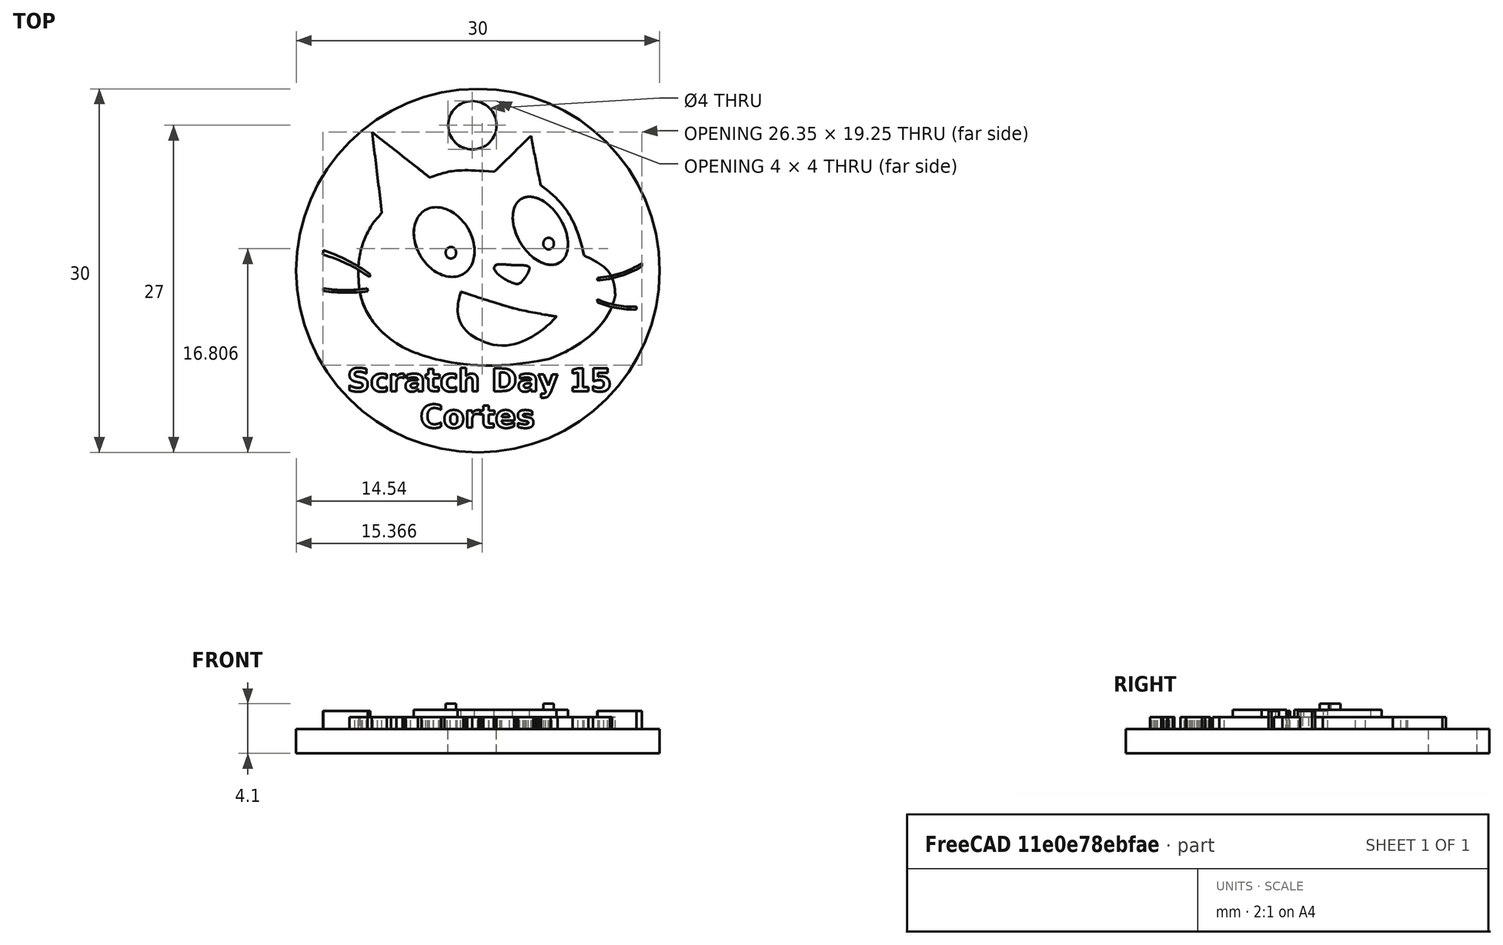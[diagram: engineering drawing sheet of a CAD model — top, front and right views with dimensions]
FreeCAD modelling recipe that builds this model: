
FCSTD DOCUMENT  (FreeCAD 0.14R3702 (Git))
Label: miscratch
License: CC-BY 3.0
LicenseURL: http://creativecommons.org/licenses/by/3.0/
objects: Part::Extrusion×9, Part::Feature×7, Part::MultiFuse×4, Part::Cylinder×2, Part::Part2DObjectPython×2, Sketcher::SketchObject×1, PartDesign::Pad×1, Part::Cut×1
note: 28 computed .brp shape members not serialized (recipe doc carries the construction recipe); baked Part::Feature solids carry a one-line shape summary decoded from their .brp

FEATURE [Part::Feature] path3150
  shape: bbox 21.31 x 19.74 x 2e-07 mm, 0 faces, 0 solids (baked)
FEATURE [Part::Feature] path3973_2
  shape: bbox 5.295 x 6.033 x 2e-07 mm, 0 faces, 0 solids (baked)
FEATURE [Part::Feature] path3981_6
  shape: bbox 4.869 x 5.906 x 2e-07 mm, 0 faces, 0 solids (baked)
FEATURE [Part::Feature] path3989_6
  shape: bbox 0.8819 x 0.9579 x 2e-07 mm, 1 faces, 0 solids (baked)
FEATURE [Part::Feature] path3985_7
  shape: bbox 0.8796 x 0.9563 x 2e-07 mm, 1 faces, 0 solids (baked)
FEATURE [Part::Feature] path4045_0
  shape: bbox 8.491 x 4.807 x 2e-07 mm, 0 faces, 0 solids (baked)
FEATURE [Part::Feature] path3993_1_6
  shape: bbox 2.935 x 1.655 x 2e-07 mm, 1 faces, 0 solids (baked)
FEATURE [Part::Extrusion] Extrude
  Base = -> path3150
  Dir = (0,0,3)
  Solid = true
FEATURE [Part::Extrusion] Extrude001
  Base = -> path3973_2
  Dir = (0,0,3.5)
  Placement = pos=(0,0,0.1) rot=(0,0,1;0rad)
  Solid = true
FEATURE [Part::Extrusion] Extrude002
  Base = -> path3981_6
  Dir = (0,0,3.5)
  Placement = pos=(0,0,0.1) rot=(0,0,1;0rad)
  Solid = true
FEATURE [Part::Extrusion] Extrude003
  Base = -> path3989_6
  Dir = (0,0,4)
  Placement = pos=(0,0,0.1) rot=(0,0,1;0rad)
  Solid = true
FEATURE [Part::Extrusion] Extrude004
  Base = -> path3985_7
  Dir = (0,0,4)
  Placement = pos=(0,0,0.1) rot=(0,0,1;0rad)
  Solid = true
FEATURE [Part::Extrusion] Extrude005
  Base = -> path4045_0
  Dir = (0,0,3.5)
  Placement = pos=(0,0,0.1) rot=(0,0,1;0rad)
  Solid = true
FEATURE [Part::Extrusion] Extrude006
  Base = -> path3993_1_6
  Dir = (0,0,3.5)
  Placement = pos=(0,0,0.1) rot=(0,0,1;0rad)
  Solid = true
FEATURE [Part::Cylinder] Cylinder  label="Cilindro"
  Angle = 360
  Height = 2
  Placement = pos=(-0.544365,0,0) rot=(0,0,1;0rad)
  Radius = 15
FEATURE [Part::MultiFuse] Fusion
  Shapes = -> [Extrude006,Extrude005,Extrude004,Extrude003,Extrude002,Extrude001]
FEATURE [Part::MultiFuse] Fusion001  label="Cara"
  Shapes = -> [Extrude,Fusion]
FEATURE [Sketcher::SketchObject] Sketch
  sketch-geometry (16):
    g0: ArcOfCircle CenterX=-17.433 CenterY=-11.1627 CenterZ=0 NormalX=0 NormalY=0 NormalZ=1 Radius=13.4853 StartAngle=0.935492 EndAngle=1.26069
    g1: ArcOfCircle CenterX=-16.3775 CenterY=-9.99206 CenterZ=0 NormalX=0 NormalY=0 NormalZ=1 Radius=11.6992 StartAngle=0.940555 EndAngle=1.30895
    g2: LineSegment StartX=-13.3491 StartY=1.30836 StartZ=0 EndX=-13.3178 EndY=1.67931 EndZ=0
    g3: LineSegment StartX=-9.48275 StartY=-0.540455 StartZ=0 EndX=-9.43055 EndY=-0.308532 EndZ=0
    g4: ArcOfCircle CenterX=-11.3327 CenterY=12.8218 CenterZ=0 NormalX=0 NormalY=0 NormalZ=1 Radius=14.6336 StartAngle=4.57669 EndAngle=4.8299
    g5: ArcOfCircle CenterX=-11.4641 CenterY=9.02572 CenterZ=0 NormalX=0 NormalY=0 NormalZ=1 Radius=10.6416 StartAngle=4.53984 EndAngle=4.88064
    g6: LineSegment StartX=-13.3123 StartY=-1.67733 StartZ=0 EndX=-13.2912 EndY=-1.45785 EndZ=0
    g7: LineSegment StartX=-9.61701 StartY=-1.71092 StartZ=0 EndX=-9.68211 EndY=-1.46561 EndZ=0
    g8: ArcOfCircle CenterX=8.83007 CenterY=7.09702 CenterZ=0 NormalX=0 NormalY=0 NormalZ=1 Radius=7.69944 StartAngle=4.77653 EndAngle=5.28472
    g9: ArcOfCircle CenterX=8.82319 CenterY=7.26907 CenterZ=0 NormalX=0 NormalY=0 NormalZ=1 Radius=8.0805 StartAngle=4.77282 EndAngle=5.25567
    g10: LineSegment StartX=9.3112 StartY=-0.796674 StartZ=0 EndX=9.32356 EndY=-0.586581 EndZ=0
    g11: LineSegment StartX=13 StartY=0.624547 StartZ=0 EndX=13.0004 EndY=0.352029 EndZ=0
    g12: ArcOfCircle CenterX=12.3215 CenterY=4.68045 CenterZ=0 NormalX=0 NormalY=0 NormalZ=1 Radius=7.66759 StartAngle=4.30717 EndAngle=4.74046
    g13: ArcOfCircle CenterX=12.3459 CenterY=4.74222 CenterZ=0 NormalX=0 NormalY=0 NormalZ=1 Radius=7.95906 StartAngle=4.32312 EndAngle=4.73791
    g14: LineSegment StartX=9.32534 StartY=-2.62139 StartZ=0 EndX=9.29884 EndY=-2.36619 EndZ=0
    g15: LineSegment StartX=12.549 StartY=-3.21425 StartZ=0 EndX=12.5367 EndY=-2.98412 EndZ=0
  constraints (16):
    c: Coincident(g1,g2)
    c: Coincident(g0,g2)
    c: Coincident(g0,g3)
    c: Coincident(g1,g3)
    c: Coincident(g6,g4)
    c: Coincident(g6,g5)
    c: Coincident(g7,g5)
    c: Coincident(g4,g7)
    c: Coincident(g10,g9)
    c: Coincident(g14,g13)
    c: Coincident(g12,g14)
    c: Coincident(g15,g13)
    c: Coincident(g12,g15)
    c: Coincident(g9,g11)
    c: Coincident(g8,g11)
    c: Coincident(g8,g10)
FEATURE [PartDesign::Pad] Pad  label="bigotes"
  Length = 3.5
  Length2 = 100
  Sketch = -> Sketch
  Type = 0
FEATURE [Part::MultiFuse] Fusion002  label="ScratchFace"
  Shapes = -> [Fusion001,Pad]
FEATURE [Part::Cylinder] Cylinder001  label="Cilindro001"
  Angle = 360
  Height = 10
  Placement = pos=(-1,12,-4) rot=(0,0,1;0rad)
  Radius = 2
FEATURE [Part::Cut] Cut  label="Base"
  Base = -> Cylinder
  Tool = -> Cylinder001
FEATURE [Part::Part2DObjectPython] ShapeString  # Draft 2D object (typed FeaturePython)
  FontFile = <path>
  Placement = pos=(-11.3,-9.94937,2) rot=(0,0,1;0rad)
  Size = 2
  String = Scratch Day 15
  Tracking = 0
FEATURE [Part::Extrusion] Extrude009  label="Texto_Scratch"
  Base = -> ShapeString
  Dir = (0,0,1)
  Solid = false
FEATURE [Part::Part2DObjectPython] ShapeString001  # Draft 2D object (typed FeaturePython)
  FontFile = <path>
  Placement = pos=(-5.3,-12.9494,2) rot=(0,0,1;0rad)
  Size = 2
  String = Cortes
  Tracking = 0
FEATURE [Part::Extrusion] Extrude010  label="Texto_Cortes"
  Base = -> ShapeString001
  Dir = (0,0,1)
  Solid = false
FEATURE [Part::MultiFuse] Fusion003  label="MedallaScratch"
  Shapes = -> [Extrude010,Cut,Fusion002,Extrude009]
note: 2 file-system paths scrubbed to <path> (originals preserved in the JSON sidecar)
